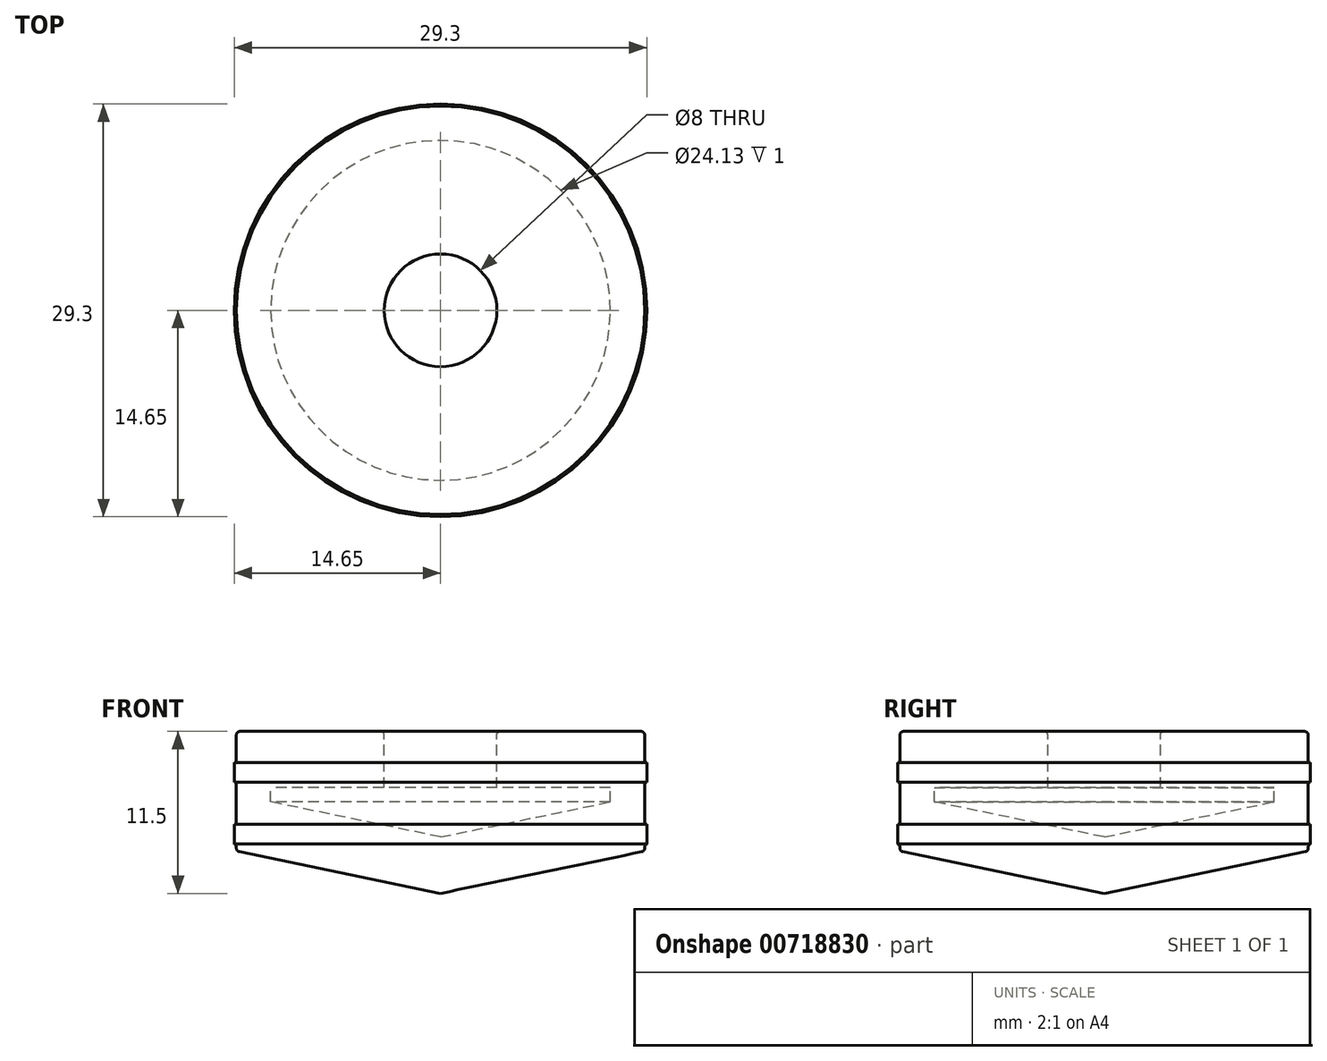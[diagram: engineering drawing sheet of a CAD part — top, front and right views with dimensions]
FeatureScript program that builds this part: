
annotation { "Feature Type Name" : "Feature", "Feature Type Description" : "" }
export const myFeature = defineFeature(function(context is Context, id is Id, definition is map)
    precondition{}
    {
        {
            var Q0;
            Q0=qCreatedBy(makeId("Front.planeOp"),FACE);
            var sketch = newSketch(context, id + "F0", { "sketchPlane" : qUnion([Q0])});
            skLineSegment(sketch, "E0", {"start": v(0, 47.92) * mm, "end": v(14.5, 50.92) * mm});
            skLineSegment(sketch, "E1", {"start": v(14.5, 50.92) * mm, "end": v(14.5, 51.42) * mm});
            skLineSegment(sketch, "E2", {"start": v(14.5, 59.42) * mm, "end": v(4, 59.42) * mm});
            skLineSegment(sketch, "E3.bottom", {"start": v(4, 55.42) * mm, "end": v(12.06, 55.42) * mm});
            skLineSegment(sketch, "E4", {"start": v(4, 59.42) * mm, "end": v(4, 55.42) * mm});
            skLineSegment(sketch, "E5", {"start": v(12.06, 54.42) * mm, "end": v(0, 51.92) * mm});
            skLineSegment(sketch, "E6", {"start": v(0, 51.92) * mm, "end": v(0, 47.92) * mm});
            skLineSegment(sketch, "E7", {"start": v(12.06, 55.42) * mm, "end": v(12.06, 54.42) * mm});
            skLineSegment(sketch, "E8.bottom", {"start": v(14.5, 57.22) * mm, "end": v(14.65, 57.22) * mm});
            skLineSegment(sketch, "E8.top", {"start": v(14.5, 55.82) * mm, "end": v(14.65, 55.82) * mm});
            skLineSegment(sketch, "E8.right", {"start": v(14.65, 57.22) * mm, "end": v(14.65, 55.82) * mm});
            skLineSegment(sketch, "E9.bottom", {"start": v(14.5, 52.82) * mm, "end": v(14.65, 52.82) * mm});
            skLineSegment(sketch, "E9.top", {"start": v(14.5, 51.42) * mm, "end": v(14.65, 51.42) * mm});
            skLineSegment(sketch, "E9.right", {"start": v(14.65, 52.82) * mm, "end": v(14.65, 51.42) * mm});
            skLineSegment(sketch, "E10.trimOffspring", {"start": v(14.5, 57.22) * mm, "end": v(14.5, 59.42) * mm});
            skLineSegment(sketch, "E11.trimOffspring", {"start": v(14.5, 52.82) * mm, "end": v(14.5, 55.82) * mm});
            skSolve(sketch);
        }
        {
            var Q0;
            Q0 = qSketchRegion(id + "F0", true);
            var Q1;
            Q1=sQuery(id+"F0.wireOp",EDGE,"E6");
            revolve(context, id + "F1", {"surfaceOperationType" : NewSurfaceOperationType.NEW, "entities" : qUnion([Q0]), "axis" : qUnion([Q1]), "revolveType" : RevolveType.FULL});
        }
        {
            var Q0;
            Q0=makeQuery(id+"F1.opRevolve","SWEPT_EDGE",EDGE,{"disambiguationData":[OSD([sQuery(id+"F0.wireOp",EDGE,"E0"),sQuery(id+"F0.wireOp",EDGE,"E1")])]});
            var Q1;
            Q1=makeQuery(id+"F1.opRevolve","SWEPT_EDGE",EDGE,{"disambiguationData":[OSD([sQuery(id+"F0.wireOp",EDGE,"E1"),sQuery(id+"F0.wireOp",EDGE,"E2")])]});
            fillet(context, id + "F2", {"entities" : qUnion([Q0, Q1]), "radius" : .25 * mm, "tangentPropagation" : true, "allowEdgeOverflow" : false});
        }
        {
            var Q0;
            Q0=makeQuery(id+"F1.opRevolve","SWEPT_EDGE",EDGE,{"disambiguationData":[OSD([sQuery(id+"F0.wireOp",EDGE,"E9.bottom"),sQuery(id+"F0.wireOp",EDGE,"E11.trimOffspring")])]});
            var Q1;
            Q1=makeQuery(id+"F1.opRevolve","SWEPT_EDGE",EDGE,{"disambiguationData":[OSD([sQuery(id+"F0.wireOp",EDGE,"E8.top"),sQuery(id+"F0.wireOp",EDGE,"E11.trimOffspring")])]});
            var Q2;
            Q2=makeQuery(id+"F1.opRevolve","SWEPT_EDGE",EDGE,{"disambiguationData":[OSD([sQuery(id+"F0.wireOp",EDGE,"E8.bottom"),sQuery(id+"F0.wireOp",EDGE,"E10.trimOffspring")])]});
            fillet(context, id + "F3", {"entities" : qUnion([Q0, Q1, Q2]), "radius" : 0.1 * mm, "tangentPropagation" : true, "allowEdgeOverflow" : false});
        }
    });
